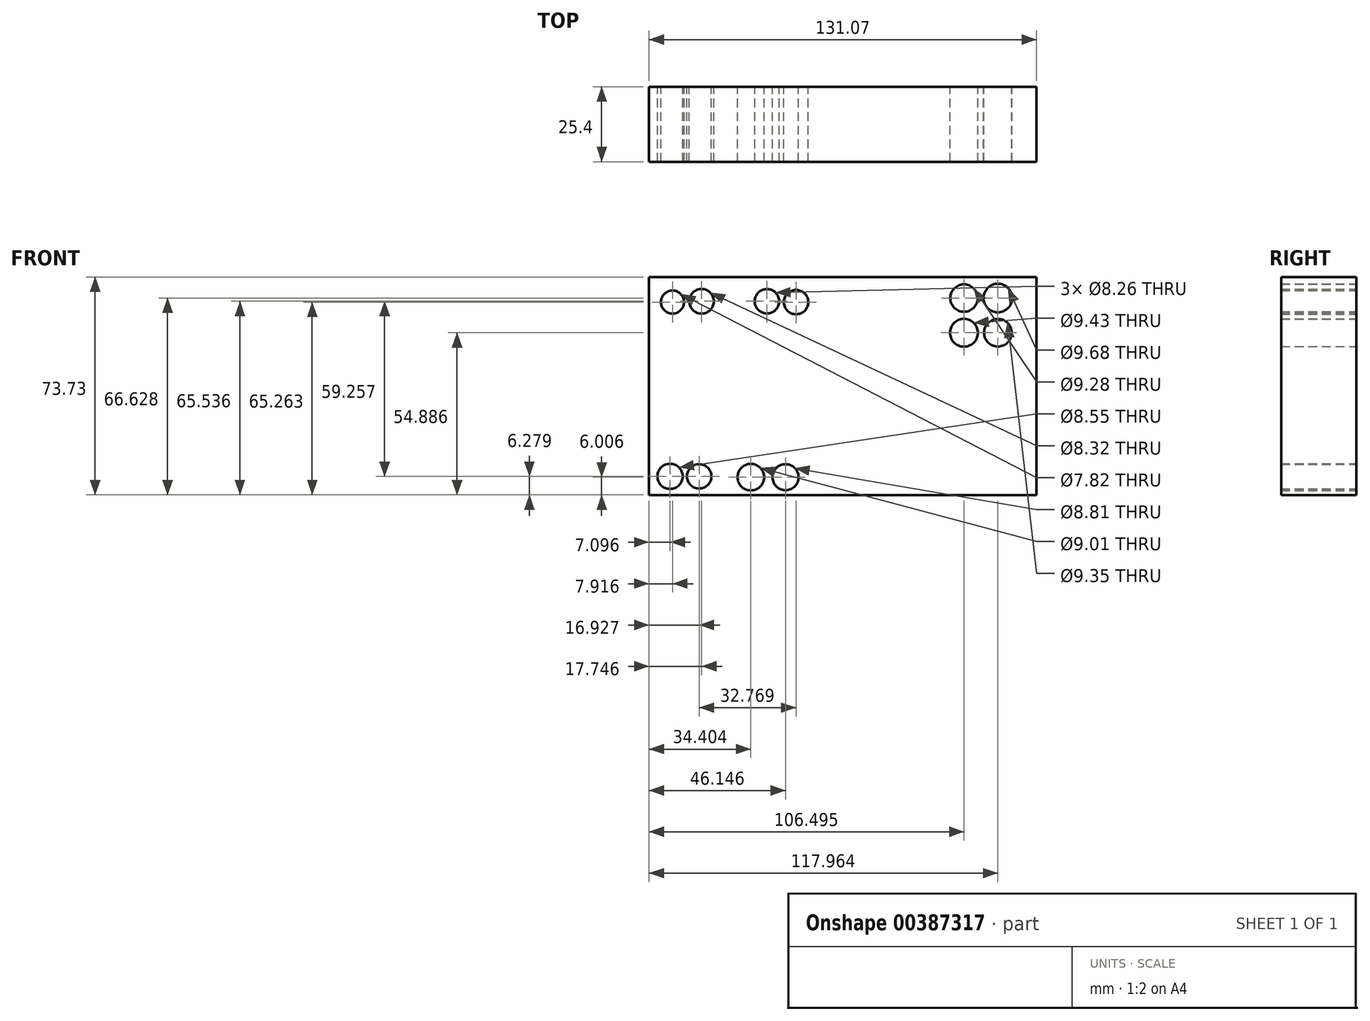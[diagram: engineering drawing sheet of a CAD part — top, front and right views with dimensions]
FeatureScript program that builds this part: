
annotation { "Feature Type Name" : "Feature", "Feature Type Description" : "" }
export const myFeature = defineFeature(function(context is Context, id is Id, definition is map)
    precondition{}
    {
        {
            var Q0;
            Q0=qCreatedBy(makeId("Front.planeOp"),FACE);
            var sketch = newSketch(context, id + "F0", { "sketchPlane" : qUnion([Q0])});
            skLineSegment(sketch, "E0.bottom", {"start": v(-62.53, -61.44) * mm, "end": v(68.54, -61.44) * mm});
            skLineSegment(sketch, "E0.top", {"start": v(-62.53, 12.29) * mm, "end": v(68.54, 12.29) * mm});
            skLineSegment(sketch, "E0.left", {"start": v(-62.53, -61.44) * mm, "end": v(-62.53, 12.29) * mm});
            skLineSegment(sketch, "E0.right", {"start": v(68.54, -61.44) * mm, "end": v(68.54, 12.29) * mm});
            skCircle(sketch, "E1", {"center": v(-22.66, 4.1) * mm, "radius": 4.13 * mm});
            skCircle(sketch, "E2", {"center": v(-28.13, -55.43) * mm, "radius": 4.5 * mm});
            skCircle(sketch, "E3", {"center": v(-16.38, -55.43) * mm, "radius": 4.4 * mm});
            skCircle(sketch, "E4", {"center": v(-54.61, 3.82) * mm, "radius": 3.9 * mm});
            skCircle(sketch, "E5", {"center": v(-44.78, 4.1) * mm, "radius": 4.16 * mm});
            skCircle(sketch, "E6", {"center": v(-12.83, 3.82) * mm, "radius": 4.13 * mm});
            skPoint(sketch, "E7.center.orphan", {"position": v(43.96, 5.19) * mm});
            skPoint(sketch, "E8.center.orphan", {"position": v(55.43, 5.19) * mm});
            skCircle(sketch, "E9", {"center": v(-45.6, -55.16) * mm, "radius": 4.13 * mm});
            skCircle(sketch, "E10", {"center": v(-55.43, -55.16) * mm, "radius": 4.27 * mm});
            skCircle(sketch, "E11", {"center": v(43.96, 5.19) * mm, "radius": 4.64 * mm});
            skCircle(sketch, "E12", {"center": v(55.43, 5.19) * mm, "radius": 4.84 * mm});
            skCircle(sketch, "E13", {"center": v(43.96, -6.55) * mm, "radius": 4.71 * mm});
            skCircle(sketch, "E14", {"center": v(55.43, -6.55) * mm, "radius": 4.67 * mm});
            skSolve(sketch);
        }
        {
            var Q0;
            Q0 = qSketchRegion(id + "F0", true);
            extrude(context, id + "F1", {"entities" : qUnion([Q0]), "depth" : 25.4 * mm});
        }
    });
